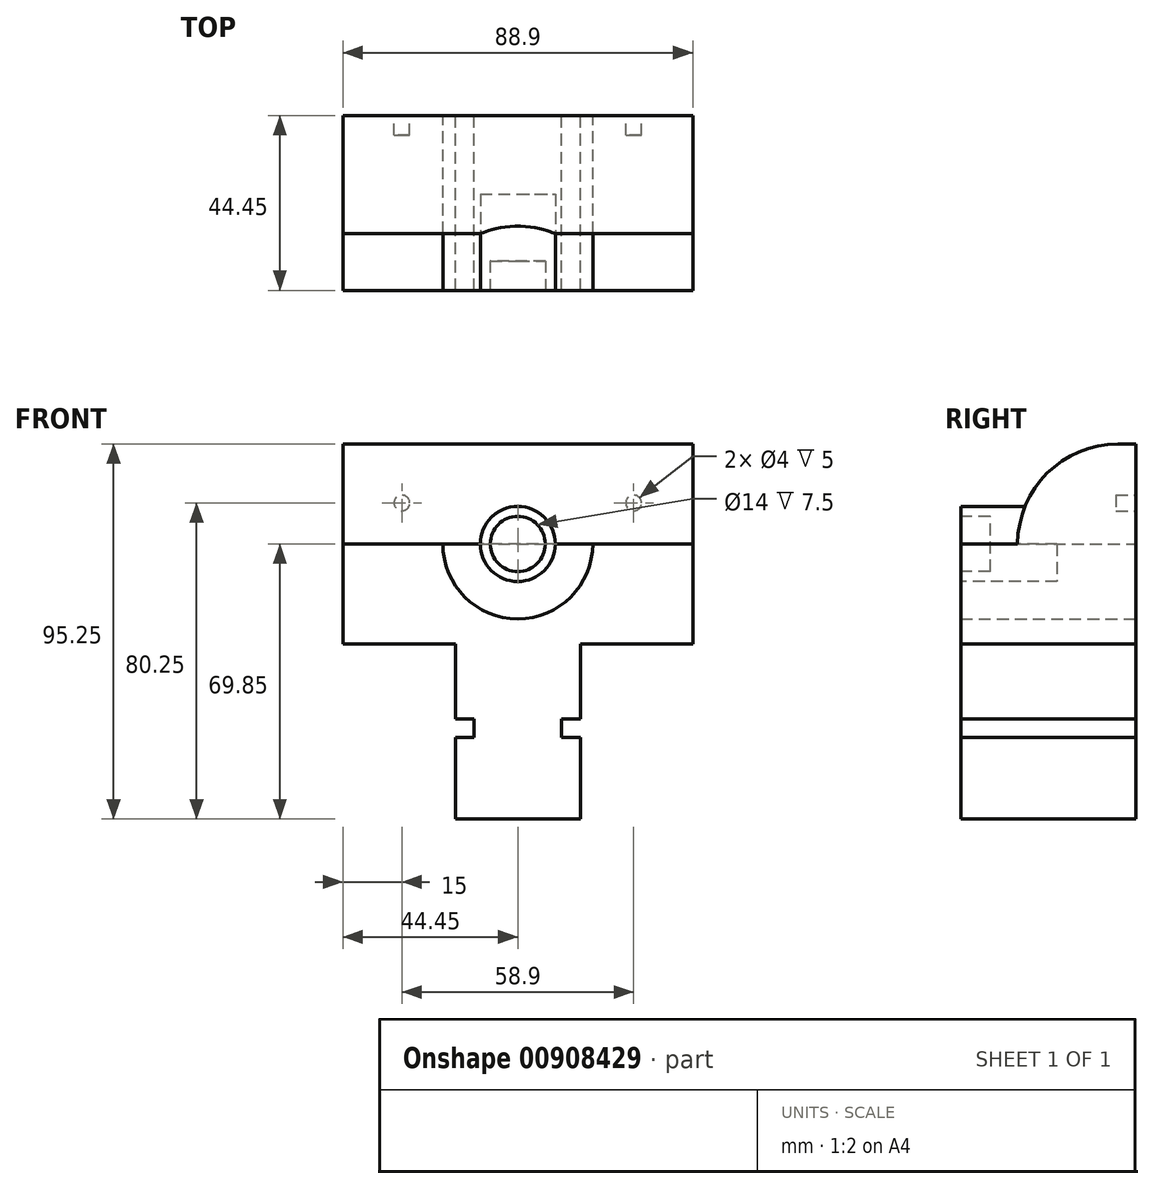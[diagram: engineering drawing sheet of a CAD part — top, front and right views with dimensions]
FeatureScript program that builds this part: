
annotation { "Feature Type Name" : "Feature", "Feature Type Description" : "" }
export const myFeature = defineFeature(function(context is Context, id is Id, definition is map)
    precondition{}
    {
        {
            var Q0;
            Q0=qCreatedBy(makeId("Front.planeOp"),FACE);
            var sketch = newSketch(context, id + "F0", { "sketchPlane" : qUnion([Q0])});
            skCircle(sketch, "E0", {"center": v(0, 0) * mm, "radius": 19.05 * mm});
            skLineSegment(sketch, "E1", {"start": v(0, 0) * mm, "end": v(-44.45, 0) * mm});
            skLineSegment(sketch, "E2", {"start": v(-44.45, 0) * mm, "end": v(44.45, 0) * mm});
            skLineSegment(sketch, "E3", {"start": v(44.45, 0) * mm, "end": v(44.45, -25.4) * mm});
            skLineSegment(sketch, "E4", {"start": v(44.45, -25.4) * mm, "end": v(15.88, -25.4) * mm});
            skLineSegment(sketch, "E5", {"start": v(-44.45, 0) * mm, "end": v(-44.45, -25.4) * mm});
            skLineSegment(sketch, "E6", {"start": v(-44.45, -25.4) * mm, "end": v(-15.87, -25.4) * mm});
            skLineSegment(sketch, "E7", {"start": v(-15.87, -25.4) * mm, "end": v(-15.87, -44.45) * mm});
            skLineSegment(sketch, "E8", {"start": v(15.88, -25.4) * mm, "end": v(15.88, -44.45) * mm});
            skLineSegment(sketch, "E9", {"start": v(-15.87, -44.45) * mm, "end": v(-11.11, -44.45) * mm});
            skLineSegment(sketch, "E10", {"start": v(15.88, -44.45) * mm, "end": v(11.11, -44.45) * mm});
            skLineSegment(sketch, "E11", {"start": v(11.11, -44.45) * mm, "end": v(11.11, -49.21) * mm});
            skLineSegment(sketch, "E12", {"start": v(11.11, -49.21) * mm, "end": v(15.88, -49.21) * mm});
            skLineSegment(sketch, "E13", {"start": v(15.88, -49.21) * mm, "end": v(15.88, -69.85) * mm});
            skLineSegment(sketch, "E14", {"start": v(15.88, -69.85) * mm, "end": v(-15.88, -69.85) * mm});
            skLineSegment(sketch, "E15", {"start": v(-11.11, -44.45) * mm, "end": v(-11.11, -49.21) * mm});
            skLineSegment(sketch, "E16", {"start": v(-11.11, -49.21) * mm, "end": v(-15.87, -49.21) * mm});
            skLineSegment(sketch, "E17", {"start": v(-15.88, -49.21) * mm, "end": v(-15.88, -69.85) * mm});
            skSolve(sketch);
        }
        {
            var Q0;
            {var subQ5=sQuery(id+"F0.wireOp",EDGE,"E3");Q0=makeQuery(id+"F0.imprint","IMPRINT",FACE,{"disambiguationData":[TD([[makeQuery(id+"F0.imprint","IMPRINT",EDGE,{"derivedFrom":subQ5}),-1.0]])]});}
            var Q1;
            {var subQ0=sQuery(id+"F0.wireOp",EDGE,"E2");var subQ4=makeQuery(id+"F0.imprint","IMPRINT",VERTEX,{"derivedFrom":subQ0});Q1=makeQuery(id+"F0.imprint","IMPRINT",FACE,{"disambiguationData":[TD([[makeQuery(id+"F0.imprint","IMPRINT",EDGE,{"disambiguationData":[TD([[subQ4,1.0]])],"derivedFrom":subQ0}),-1.0]])]});}
            var Q2;
            {var subQ0=sQuery(id+"F0.wireOp",EDGE,"E2");var subQ4=makeQuery(id+"F0.imprint","IMPRINT",VERTEX,{"derivedFrom":subQ0});Q2=makeQuery(id+"F0.imprint","IMPRINT",FACE,{"disambiguationData":[TD([[makeQuery(id+"F0.imprint","IMPRINT",EDGE,{"disambiguationData":[TD([[subQ4,1.0]])],"derivedFrom":subQ0}),1.0]])]});}
            extrude(context, id + "F1", {"entities" : qUnion([Q0, Q1, Q2]), "depth" : 44.45 * mm, "offsetDistance" : 25 * mm});
        }
        {
            var Q0;
            Q0=makeQuery(id+"F1.opExtrude","SWEPT_FACE",FACE,{"disambiguationData":[OSD([sQuery(id+"F0.wireOp",EDGE,"E5")])]});
            var sketch = newSketch(context, id + "F2", { "sketchPlane" : qUnion([Q0])});
            skLineSegment(sketch, "E18", {"start": v(0, -25.4) * mm, "end": v(0, 25.4) * mm});
            skLineSegment(sketch, "E19", {"start": v(0, 25.4) * mm, "end": v(30, 25.4) * mm});
            skLineSegment(sketch, "E20", {"start": v(30, 25.4) * mm, "end": v(30, 0) * mm});
            skLineSegment(sketch, "E21", {"start": v(30, 0) * mm, "end": v(0, 0) * mm});
            skSolve(sketch);
        }
        {
            var Q0;
            {var subQ2=sQuery(id+"F2.wireOp",EDGE,"E19");Q0=makeQuery(id+"F2.imprint","IMPRINT",FACE,{"disambiguationData":[TD([[makeQuery(id+"F2.imprint","IMPRINT",EDGE,{"derivedFrom":subQ2}),-1.0]])]});}
            extrude(context, id + "F3", {"entities" : qUnion([Q0]), "operationType" : NewBodyOperationType.ADD, "oppositeDirection" : true, "depth" : 88.9 * mm, "offsetDistance" : 25 * mm});
        }
        {
            var Q0;
            Q0=makeQuery(id+"F3.opExtrude","SWEPT_EDGE",EDGE,{"disambiguationData":[OSD([sQuery(id+"F2.wireOp",EDGE,"E19"),sQuery(id+"F2.wireOp",EDGE,"E20")])]});
            fillet(context, id + "F4", {"entities" : qUnion([Q0]), "radius" : 25.5 * mm, "tangentPropagation" : true, "allowEdgeOverflow" : false});
        }
        {
            var Q0;
            Q0=makeQuery(id+"F1.opExtrude","CAP_FACE",FACE,{"disambiguationData":[OSD([sQuery(id+"F0.wireOp",EDGE,"E0"),sQuery(id+"F0.wireOp",EDGE,"E2"),sQuery(id+"F0.wireOp",EDGE,"E3"),sQuery(id+"F0.wireOp",EDGE,"E4"),sQuery(id+"F0.wireOp",EDGE,"E5"),sQuery(id+"F0.wireOp",EDGE,"E6"),sQuery(id+"F0.wireOp",EDGE,"E7"),sQuery(id+"F0.wireOp",EDGE,"E8"),sQuery(id+"F0.wireOp",EDGE,"E9"),sQuery(id+"F0.wireOp",EDGE,"E10"),sQuery(id+"F0.wireOp",EDGE,"E11"),sQuery(id+"F0.wireOp",EDGE,"E12"),sQuery(id+"F0.wireOp",EDGE,"E13"),sQuery(id+"F0.wireOp",EDGE,"E14"),sQuery(id+"F0.wireOp",EDGE,"E15"),sQuery(id+"F0.wireOp",EDGE,"E16"),sQuery(id+"F0.wireOp",EDGE,"E17")])],"isStart":false});
            var sketch = newSketch(context, id + "F5", { "sketchPlane" : qUnion([Q0])});
            skCircle(sketch, "E22", {"center": v(0, 0) * mm, "radius": 9.53 * mm});
            skSolve(sketch);
        }
        {
            var Q0;
            Q0=makeQuery(id+"F5.imprint","IMPRINT",FACE,{"disambiguationData":[TD([[makeQuery(id+"F5.imprint","IMPRINT",EDGE,{"derivedFrom":sQuery(id+"F5.wireOp",EDGE,"E22")}),1.0]])]});
            extrude(context, id + "F6", {"entities" : qUnion([Q0]), "operationType" : NewBodyOperationType.REMOVE, "oppositeDirection" : true, "depth" : 12.7 * mm, "offsetDistance" : 25 * mm});
        }
        {
            var Q0;
            Q0=makeQuery(id+"F3.boolean.opBoolean","MERGE",FACE,{"derivedFrom":[makeQuery(id+"F1.opExtrude","CAP_FACE",FACE,{"disambiguationData":[OSD([sQuery(id+"F0.wireOp",EDGE,"E0"),sQuery(id+"F0.wireOp",EDGE,"E2"),sQuery(id+"F0.wireOp",EDGE,"E3"),sQuery(id+"F0.wireOp",EDGE,"E4"),sQuery(id+"F0.wireOp",EDGE,"E5"),sQuery(id+"F0.wireOp",EDGE,"E6"),sQuery(id+"F0.wireOp",EDGE,"E7"),sQuery(id+"F0.wireOp",EDGE,"E8"),sQuery(id+"F0.wireOp",EDGE,"E9"),sQuery(id+"F0.wireOp",EDGE,"E10"),sQuery(id+"F0.wireOp",EDGE,"E11"),sQuery(id+"F0.wireOp",EDGE,"E12"),sQuery(id+"F0.wireOp",EDGE,"E13"),sQuery(id+"F0.wireOp",EDGE,"E14"),sQuery(id+"F0.wireOp",EDGE,"E15"),sQuery(id+"F0.wireOp",EDGE,"E16"),sQuery(id+"F0.wireOp",EDGE,"E17")])],"isStart":true}),makeQuery(id+"F3.opExtrude","SWEPT_FACE",FACE,{"disambiguationData":[OSD([sQuery(id+"F2.wireOp",EDGE,"E18")])]})]});
            var sketch = newSketch(context, id + "F7", { "sketchPlane" : qUnion([Q0])});
            skLineSegment(sketch, "E23", {"start": v(-44.45, 25.4) * mm, "end": v(-44.45, 10.4) * mm});
            skLineSegment(sketch, "E24", {"start": v(-44.45, 10.4) * mm, "end": v(-29.45, 10.4) * mm});
            skCircle(sketch, "E25", {"center": v(-29.45, 10.4) * mm, "radius": 2 * mm});
            skLineSegment(sketch, "E26", {"start": v(44.45, 25.4) * mm, "end": v(44.45, 10.4) * mm});
            skLineSegment(sketch, "E27", {"start": v(44.45, 10.4) * mm, "end": v(29.45, 10.4) * mm});
            skCircle(sketch, "E28", {"center": v(29.45, 10.4) * mm, "radius": 2 * mm});
            skSolve(sketch);
        }
        {
            var Q0;
            Q0=makeQuery(id+"F7.imprint","IMPRINT",FACE,{"disambiguationData":[TD([[makeQuery(id+"F7.imprint","IMPRINT",EDGE,{"derivedFrom":sQuery(id+"F7.wireOp",EDGE,"E25")}),1.0]])]});
            var Q1;
            Q1=makeQuery(id+"F7.imprint","IMPRINT",FACE,{"disambiguationData":[TD([[makeQuery(id+"F7.imprint","IMPRINT",EDGE,{"derivedFrom":sQuery(id+"F7.wireOp",EDGE,"E28")}),1.0]])]});
            extrude(context, id + "F8", {"entities" : qUnion([Q0, Q1]), "operationType" : NewBodyOperationType.REMOVE, "oppositeDirection" : true, "depth" : 5 * mm, "offsetDistance" : 25 * mm});
        }
        {
            var Q0;
            Q0=makeQuery(id+"F1.opExtrude","CAP_FACE",FACE,{"disambiguationData":[OSD([sQuery(id+"F0.wireOp",EDGE,"E0"),sQuery(id+"F0.wireOp",EDGE,"E2"),sQuery(id+"F0.wireOp",EDGE,"E3"),sQuery(id+"F0.wireOp",EDGE,"E4"),sQuery(id+"F0.wireOp",EDGE,"E5"),sQuery(id+"F0.wireOp",EDGE,"E6"),sQuery(id+"F0.wireOp",EDGE,"E7"),sQuery(id+"F0.wireOp",EDGE,"E8"),sQuery(id+"F0.wireOp",EDGE,"E9"),sQuery(id+"F0.wireOp",EDGE,"E10"),sQuery(id+"F0.wireOp",EDGE,"E11"),sQuery(id+"F0.wireOp",EDGE,"E12"),sQuery(id+"F0.wireOp",EDGE,"E13"),sQuery(id+"F0.wireOp",EDGE,"E14"),sQuery(id+"F0.wireOp",EDGE,"E15"),sQuery(id+"F0.wireOp",EDGE,"E16"),sQuery(id+"F0.wireOp",EDGE,"E17")])],"isStart":false});
            var sketch = newSketch(context, id + "F9", { "sketchPlane" : qUnion([Q0])});
            skCircle(sketch, "E29", {"center": v(0, 0) * mm, "radius": 9.53 * mm});
            skSolve(sketch);
        }
        {
            var Q0;
            Q0=makeQuery(id+"F9.imprint","IMPRINT",FACE,{"disambiguationData":[TD([[makeQuery(id+"F9.imprint","IMPRINT",EDGE,{"derivedFrom":sQuery(id+"F9.wireOp",EDGE,"E29")}),1.0]])]});
            extrude(context, id + "F10", {"entities" : qUnion([Q0]), "operationType" : NewBodyOperationType.ADD, "oppositeDirection" : true, "depth" : 24.5 * mm, "offsetDistance" : 25 * mm});
        }
        {
            var Q0;
            Q0=makeQuery(id+"F10.boolean.opBoolean","MERGE",FACE,{"derivedFrom":[makeQuery(id+"F1.opExtrude","CAP_FACE",FACE,{"disambiguationData":[OSD([sQuery(id+"F0.wireOp",EDGE,"E0"),sQuery(id+"F0.wireOp",EDGE,"E2"),sQuery(id+"F0.wireOp",EDGE,"E3"),sQuery(id+"F0.wireOp",EDGE,"E4"),sQuery(id+"F0.wireOp",EDGE,"E5"),sQuery(id+"F0.wireOp",EDGE,"E6"),sQuery(id+"F0.wireOp",EDGE,"E7"),sQuery(id+"F0.wireOp",EDGE,"E8"),sQuery(id+"F0.wireOp",EDGE,"E9"),sQuery(id+"F0.wireOp",EDGE,"E10"),sQuery(id+"F0.wireOp",EDGE,"E11"),sQuery(id+"F0.wireOp",EDGE,"E12"),sQuery(id+"F0.wireOp",EDGE,"E13"),sQuery(id+"F0.wireOp",EDGE,"E14"),sQuery(id+"F0.wireOp",EDGE,"E15"),sQuery(id+"F0.wireOp",EDGE,"E16"),sQuery(id+"F0.wireOp",EDGE,"E17")])],"isStart":false}),makeQuery(id+"F10.opExtrude","CAP_FACE",FACE,{"disambiguationData":[OSD([sQuery(id+"F9.wireOp",EDGE,"E29")])],"isStart":true})]});
            var sketch = newSketch(context, id + "F11", { "sketchPlane" : qUnion([Q0])});
            skCircle(sketch, "E30", {"center": v(0, 0) * mm, "radius": 7 * mm});
            skSolve(sketch);
        }
        {
            var Q0;
            Q0=makeQuery(id+"F11.imprint","IMPRINT",FACE,{"disambiguationData":[TD([[makeQuery(id+"F11.imprint","IMPRINT",EDGE,{"derivedFrom":sQuery(id+"F11.wireOp",EDGE,"E30")}),1.0]])]});
            extrude(context, id + "F12", {"entities" : qUnion([Q0]), "operationType" : NewBodyOperationType.REMOVE, "oppositeDirection" : true, "depth" : 7.5 * mm, "offsetDistance" : 25 * mm});
        }
    });
